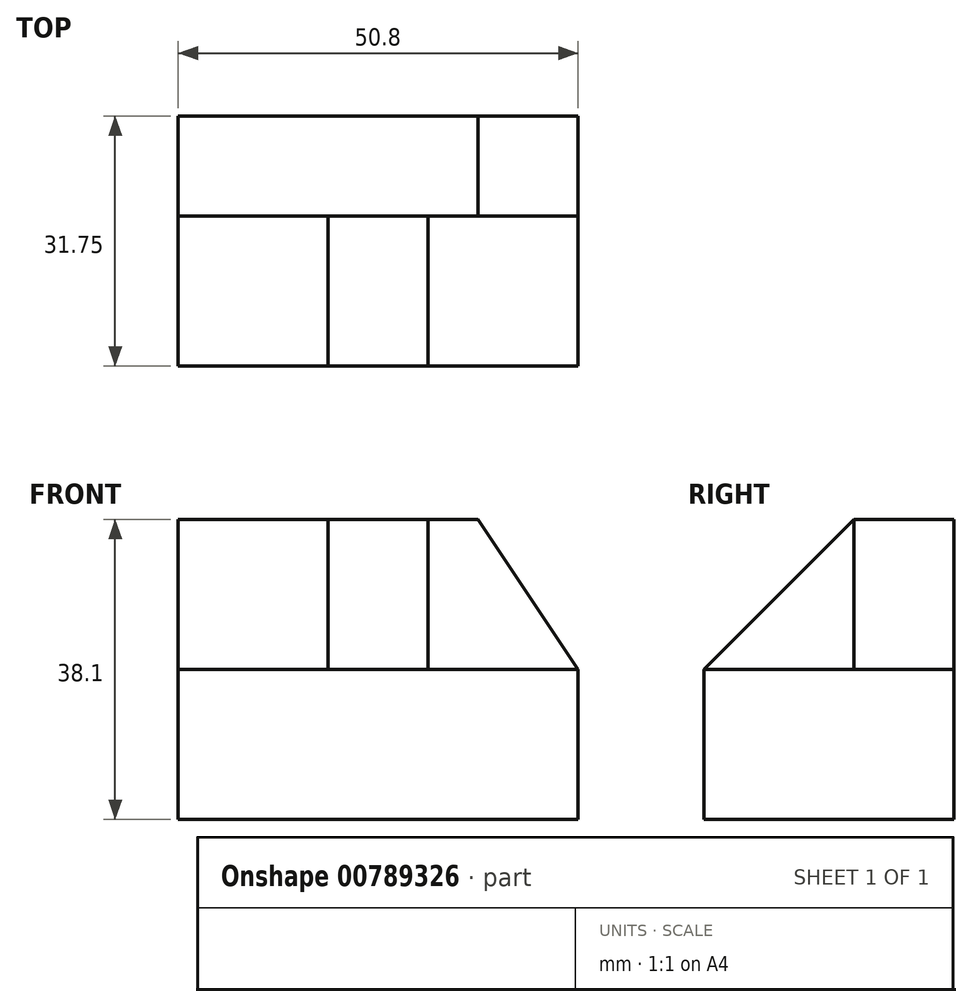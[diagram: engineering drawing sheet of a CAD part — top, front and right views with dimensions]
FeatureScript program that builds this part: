
annotation { "Feature Type Name" : "Feature", "Feature Type Description" : "" }
export const myFeature = defineFeature(function(context is Context, id is Id, definition is map)
    precondition{}
    {
        {
            var Q0;
            Q0=qCreatedBy(makeId("Front.planeOp"),FACE);
            var sketch = newSketch(context, id + "F0", { "sketchPlane" : qUnion([Q0])});
            skLineSegment(sketch, "E0", {"start": v(0, 0) * mm, "end": v(50.8, 0) * mm});
            skLineSegment(sketch, "E1", {"start": v(50.8, 0) * mm, "end": v(50.8, 38.1) * mm});
            skLineSegment(sketch, "E2", {"start": v(50.8, 38.1) * mm, "end": v(0, 38.1) * mm});
            skLineSegment(sketch, "E3", {"start": v(0, 38.1) * mm, "end": v(0, 0) * mm});
            skSolve(sketch);
        }
        {
            var Q0;
            Q0=makeQuery(id+"F0.imprint","IMPRINT",FACE,{"disambiguationData":[TD([[makeQuery(id+"F0.imprint","IMPRINT",EDGE,{"derivedFrom":sQuery(id+"F0.wireOp",EDGE,"E0")}),1.0]])]});
            extrude(context, id + "F1", {"entities" : qUnion([Q0]), "depth" : 31.75 * mm, "offsetDistance" : 25.4 * mm});
        }
        {
            var Q0;
            Q0=makeQuery(id+"F1.opExtrude","CAP_FACE",FACE,{"disambiguationData":[OSD([sQuery(id+"F0.wireOp",EDGE,"E0"),sQuery(id+"F0.wireOp",EDGE,"E1"),sQuery(id+"F0.wireOp",EDGE,"E2"),sQuery(id+"F0.wireOp",EDGE,"E3")])],"isStart":false});
            var sketch = newSketch(context, id + "F2", { "sketchPlane" : qUnion([Q0])});
            skLineSegment(sketch, "E4", {"start": v(50.8, 38.1) * mm, "end": v(31.75, 38.1) * mm});
            skLineSegment(sketch, "E5", {"start": v(31.75, 38.1) * mm, "end": v(31.75, 19.05) * mm});
            skLineSegment(sketch, "E6", {"start": v(31.75, 19.05) * mm, "end": v(50.8, 19.05) * mm});
            skLineSegment(sketch, "E7", {"start": v(50.8, 19.05) * mm, "end": v(50.8, 38.1) * mm});
            skLineSegment(sketch, "E8", {"start": v(0, 38.1) * mm, "end": v(19.05, 38.1) * mm});
            skLineSegment(sketch, "E9", {"start": v(19.05, 38.1) * mm, "end": v(19.05, 19.05) * mm});
            skLineSegment(sketch, "E10", {"start": v(19.05, 19.05) * mm, "end": v(0, 19.05) * mm});
            skSolve(sketch);
        }
        {
            var Q0;
            Q0=makeQuery(id+"F2.imprint","IMPRINT",FACE,{"disambiguationData":[TD([[makeQuery(id+"F2.imprint","IMPRINT",EDGE,{"derivedFrom":sQuery(id+"F2.wireOp",EDGE,"E4")}),1.0]])]});
            var Q1;
            {var subQ0=sQuery(id+"F2.wireOp",EDGE,"E8");Q1=makeQuery(id+"F2.imprint","IMPRINT",FACE,{"disambiguationData":[TD([[makeQuery(id+"F2.imprint","IMPRINT",EDGE,{"derivedFrom":subQ0}),1.0]])]});}
            extrude(context, id + "F3", {"entities" : qUnion([Q0, Q1]), "operationType" : NewBodyOperationType.REMOVE, "oppositeDirection" : true, "depth" : 19.05 * mm, "offsetDistance" : 25.4 * mm});
        }
        {
            var Q0;
            Q0=makeQuery(id+"F3.boolean.opBoolean","COPY",FACE,{"derivedFrom":makeQuery(id+"F3.opExtrude","SWEPT_FACE",FACE,{"disambiguationData":[OSD([sQuery(id+"F2.wireOp",EDGE,"E5")])]})});
            var sketch = newSketch(context, id + "F4", { "sketchPlane" : qUnion([Q0])});
            skLineSegment(sketch, "E11", {"start": v(-12.7, 38.1) * mm, "end": v(-31.75, 19.05) * mm});
            skSolve(sketch);
        }
        {
            var Q0;
            Q0=makeQuery(id+"F4.imprint","IMPRINT",FACE,{"disambiguationData":[TD([[makeQuery(id+"F4.imprint","IMPRINT",EDGE,{"derivedFrom":sQuery(id+"F4.wireOp",EDGE,"E11")}),-1.0]])]});
            extrude(context, id + "F5", {"entities" : qUnion([Q0]), "operationType" : NewBodyOperationType.REMOVE, "endBound" : BoundingType.UP_TO_NEXT, "oppositeDirection" : true, "depth" : 25.4 * mm, "offsetDistance" : 25.4 * mm});
        }
        {
            var Q0;
            Q0=makeQuery(id+"F3.boolean.opBoolean","COPY",FACE,{"derivedFrom":makeQuery(id+"F3.opExtrude","CAP_FACE",FACE,{"disambiguationData":[OSD([sQuery(id+"F2.wireOp",EDGE,"E4"),sQuery(id+"F2.wireOp",EDGE,"E5"),sQuery(id+"F2.wireOp",EDGE,"E6"),sQuery(id+"F2.wireOp",EDGE,"E7")])],"isStart":false})});
            var sketch = newSketch(context, id + "F6", { "sketchPlane" : qUnion([Q0])});
            skLineSegment(sketch, "E12", {"start": v(31.75, 38.1) * mm, "end": v(38.1, 38.1) * mm});
            skLineSegment(sketch, "E13", {"start": v(38.1, 38.1) * mm, "end": v(50.8, 19.05) * mm});
            skSolve(sketch);
        }
        {
            var Q0;
            {var subQ0=sQuery(id+"F6.wireOp",EDGE,"E13");Q0=makeQuery(id+"F6.imprint","IMPRINT",FACE,{"disambiguationData":[TD([[makeQuery(id+"F6.imprint","IMPRINT",EDGE,{"derivedFrom":subQ0}),1.0]])]});}
            extrude(context, id + "F7", {"entities" : qUnion([Q0]), "operationType" : NewBodyOperationType.REMOVE, "endBound" : BoundingType.UP_TO_NEXT, "oppositeDirection" : true, "depth" : 25.4 * mm, "offsetDistance" : 25.4 * mm});
        }
    });
